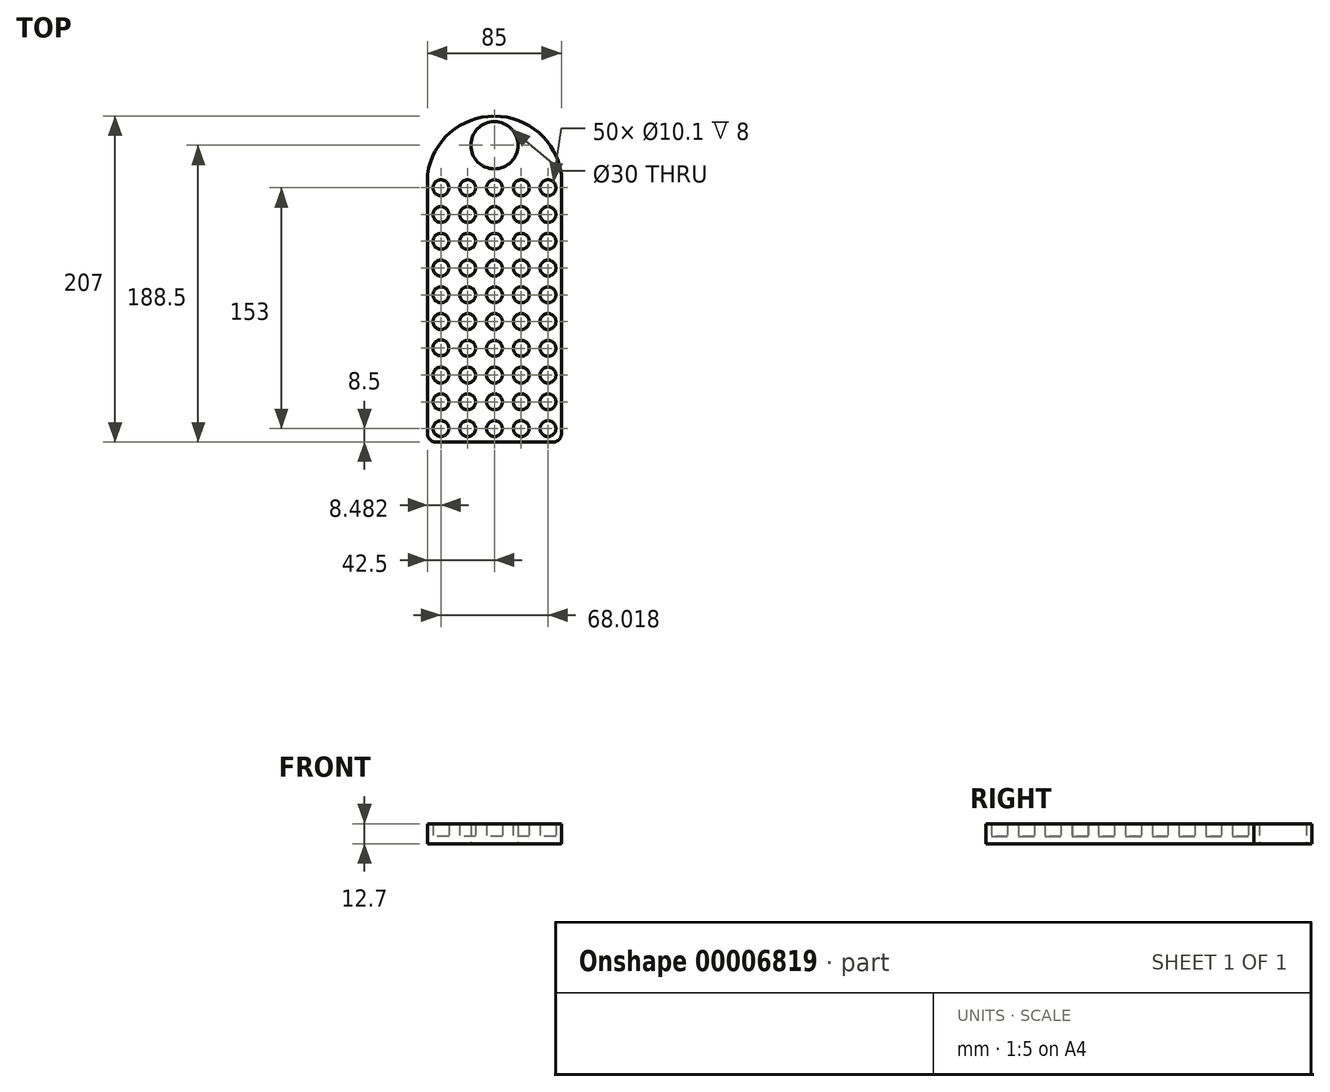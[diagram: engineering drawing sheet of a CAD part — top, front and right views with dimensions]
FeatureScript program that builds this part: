
annotation { "Feature Type Name" : "Feature", "Feature Type Description" : "" }
export const myFeature = defineFeature(function(context is Context, id is Id, definition is map)
    precondition{}
    {
        {
            var Q0;
            Q0=qCreatedBy(makeId("Top.planeOp"),FACE);
            var sketch = newSketch(context, id + "F0", { "sketchPlane" : qUnion([Q0])});
            skLineSegment(sketch, "E0", {"start": v(0, 0) * mm, "end": v(8.5, 0) * mm, "construction": true});
            skLineSegment(sketch, "E1", {"start": v(8.5, 0) * mm, "end": v(25.5, 0) * mm, "construction": true});
            skLineSegment(sketch, "E2", {"start": v(25.5, 0) * mm, "end": v(25.5, 0) * mm});
            skLineSegment(sketch, "E3", {"start": v(25.5, 0) * mm, "end": v(42.5, 0) * mm, "construction": true});
            skLineSegment(sketch, "E4", {"start": v(42.5, 0) * mm, "end": v(42.5, 0) * mm});
            skLineSegment(sketch, "E5", {"start": v(0, 0) * mm, "end": v(0, 8.5) * mm, "construction": true});
            skLineSegment(sketch, "E6", {"start": v(42.5, 0) * mm, "end": v(59.5, 0) * mm, "construction": true});
            skLineSegment(sketch, "E7", {"start": v(0, 8.5) * mm, "end": v(59.5, 8.5) * mm, "construction": true});
            skLineSegment(sketch, "E8", {"start": v(8.5, 0) * mm, "end": v(8.5, 8.5) * mm, "construction": true});
            skLineSegment(sketch, "E9", {"start": v(25.5, 0) * mm, "end": v(25.5, 8.5) * mm, "construction": true});
            skLineSegment(sketch, "E10", {"start": v(42.5, 0) * mm, "end": v(42.5, 8.5) * mm, "construction": true});
            skLineSegment(sketch, "E11", {"start": v(59.5, 0) * mm, "end": v(59.5, 8.5) * mm, "construction": true});
            skCircle(sketch, "E12", {"center": v(8.5, 8.5) * mm, "radius": 5.05 * mm});
            skLineSegment(sketch, "E13", {"start": v(59.5, 0) * mm, "end": v(76.5, 0) * mm, "construction": true});
            skLineSegment(sketch, "E14", {"start": v(59.5, 8.5) * mm, "end": v(76.5, 8.5) * mm, "construction": true});
            skLineSegment(sketch, "E15", {"start": v(76.5, 0) * mm, "end": v(76.5, 8.5) * mm, "construction": true});
            skCircle(sketch, "E16", {"center": v(25.5, 8.5) * mm, "radius": 5.05 * mm});
            skCircle(sketch, "E17", {"center": v(42.5, 8.5) * mm, "radius": 5.05 * mm});
            skCircle(sketch, "E18", {"center": v(59.5, 8.5) * mm, "radius": 5.05 * mm});
            skLineSegment(sketch, "E19", {"start": v(76.5, 0) * mm, "end": v(85, 0) * mm, "construction": true});
            skLineSegment(sketch, "E20", {"start": v(85, 8.5) * mm, "end": v(76.5, 8.5) * mm, "construction": true});
            skLineSegment(sketch, "E21", {"start": v(85, 0) * mm, "end": v(85, 8.5) * mm});
            skCircle(sketch, "E22", {"center": v(76.5, 8.5) * mm, "radius": 5.05 * mm});
            skLineSegment(sketch, "E23", {"start": v(0, 8.5) * mm, "end": v(0, 25.5) * mm, "construction": true});
            skLineSegment(sketch, "E24", {"start": v(0, 25.5) * mm, "end": v(85, 25.5) * mm, "construction": true});
            skLineSegment(sketch, "E25", {"start": v(8.5, 8.5) * mm, "end": v(8.5, 25.5) * mm, "construction": true});
            skLineSegment(sketch, "E26", {"start": v(25.5, 8.5) * mm, "end": v(25.5, 25.5) * mm, "construction": true});
            skLineSegment(sketch, "E27", {"start": v(42.5, 8.5) * mm, "end": v(42.5, 25.5) * mm, "construction": true});
            skLineSegment(sketch, "E28", {"start": v(59.5, 8.5) * mm, "end": v(59.5, 25.5) * mm, "construction": true});
            skLineSegment(sketch, "E29", {"start": v(76.5, 8.5) * mm, "end": v(76.5, 25.5) * mm, "construction": true});
            skLineSegment(sketch, "E30", {"start": v(85, 8.5) * mm, "end": v(85, 25.5) * mm, "construction": true});
            skCircle(sketch, "E31", {"center": v(8.5, 25.5) * mm, "radius": 5.05 * mm});
            skCircle(sketch, "E32", {"center": v(25.5, 25.5) * mm, "radius": 5.05 * mm});
            skCircle(sketch, "E33", {"center": v(42.5, 25.5) * mm, "radius": 5.05 * mm});
            skCircle(sketch, "E34", {"center": v(59.5, 25.5) * mm, "radius": 5.05 * mm});
            skCircle(sketch, "E35", {"center": v(76.5, 25.5) * mm, "radius": 5.05 * mm});
            skLineSegment(sketch, "E36", {"start": v(0, 25.5) * mm, "end": v(0, 42.5) * mm, "construction": true});
            skLineSegment(sketch, "E37", {"start": v(0, 42.5) * mm, "end": v(85, 42.5) * mm, "construction": true});
            skLineSegment(sketch, "E38", {"start": v(85, 25.5) * mm, "end": v(85, 42.5) * mm, "construction": true});
            skLineSegment(sketch, "E39", {"start": v(76.5, 25.5) * mm, "end": v(76.5, 42.5) * mm, "construction": true});
            skLineSegment(sketch, "E40", {"start": v(59.5, 25.5) * mm, "end": v(59.5, 42.5) * mm, "construction": true});
            skLineSegment(sketch, "E41", {"start": v(42.5, 25.5) * mm, "end": v(42.5, 42.5) * mm, "construction": true});
            skLineSegment(sketch, "E42", {"start": v(25.5, 25.5) * mm, "end": v(25.5, 42.5) * mm, "construction": true});
            skLineSegment(sketch, "E43", {"start": v(8.5, 25.5) * mm, "end": v(8.5, 42.5) * mm, "construction": true});
            skLineSegment(sketch, "E44", {"start": v(0, 42.5) * mm, "end": v(0, 59.5) * mm, "construction": true});
            skLineSegment(sketch, "E45", {"start": v(0, 59.5) * mm, "end": v(85, 59.5) * mm, "construction": true});
            skLineSegment(sketch, "E46", {"start": v(85, 42.5) * mm, "end": v(85, 59.5) * mm, "construction": true});
            skLineSegment(sketch, "E47", {"start": v(76.5, 42.5) * mm, "end": v(76.5, 59.5) * mm, "construction": true});
            skLineSegment(sketch, "E48", {"start": v(59.5, 42.5) * mm, "end": v(59.5, 59.5) * mm, "construction": true});
            skLineSegment(sketch, "E49", {"start": v(42.5, 42.5) * mm, "end": v(42.5, 59.5) * mm, "construction": true});
            skLineSegment(sketch, "E50", {"start": v(25.5, 42.5) * mm, "end": v(25.5, 59.5) * mm, "construction": true});
            skLineSegment(sketch, "E51", {"start": v(8.5, 42.5) * mm, "end": v(8.5, 59.5) * mm, "construction": true});
            skLineSegment(sketch, "E52", {"start": v(0, 59.5) * mm, "end": v(0, 76.5) * mm, "construction": true});
            skLineSegment(sketch, "E53", {"start": v(0, 76.5) * mm, "end": v(84.97, 76.5) * mm, "construction": true});
            skLineSegment(sketch, "E54", {"start": v(8.5, 59.5) * mm, "end": v(8.5, 76.5) * mm, "construction": true});
            skLineSegment(sketch, "E55", {"start": v(25.5, 59.5) * mm, "end": v(25.5, 76.5) * mm, "construction": true});
            skLineSegment(sketch, "E56", {"start": v(42.5, 59.5) * mm, "end": v(42.5, 76.5) * mm, "construction": true});
            skLineSegment(sketch, "E57", {"start": v(59.5, 59.5) * mm, "end": v(59.5, 76.5) * mm, "construction": true});
            skLineSegment(sketch, "E58", {"start": v(76.5, 59.5) * mm, "end": v(76.5, 76.5) * mm, "construction": true});
            skLineSegment(sketch, "E59", {"start": v(85, 59.5) * mm, "end": v(85, 76.5) * mm, "construction": true});
            skCircle(sketch, "E60", {"center": v(8.5, 42.5) * mm, "radius": 5.05 * mm});
            skCircle(sketch, "E61", {"center": v(8.48, 59.8) * mm, "radius": 5.05 * mm});
            skCircle(sketch, "E62", {"center": v(8.5, 76.5) * mm, "radius": 5.05 * mm});
            skCircle(sketch, "E63", {"center": v(25.5, 76.5) * mm, "radius": 5.05 * mm});
            skCircle(sketch, "E64", {"center": v(25.5, 59.5) * mm, "radius": 5.05 * mm});
            skCircle(sketch, "E65", {"center": v(25.5, 42.5) * mm, "radius": 5.05 * mm});
            skCircle(sketch, "E66", {"center": v(42.5, 76.5) * mm, "radius": 5.05 * mm});
            skCircle(sketch, "E67", {"center": v(42.5, 59.5) * mm, "radius": 5.05 * mm});
            skCircle(sketch, "E68", {"center": v(42.5, 42.5) * mm, "radius": 5.05 * mm});
            skCircle(sketch, "E69", {"center": v(59.5, 42.5) * mm, "radius": 5.05 * mm});
            skCircle(sketch, "E70", {"center": v(59.5, 59.5) * mm, "radius": 5.05 * mm});
            skCircle(sketch, "E71", {"center": v(59.5, 76.5) * mm, "radius": 5.05 * mm});
            skCircle(sketch, "E72", {"center": v(76.5, 76.5) * mm, "radius": 5.05 * mm});
            skCircle(sketch, "E73", {"center": v(76.5, 59.5) * mm, "radius": 5.05 * mm});
            skCircle(sketch, "E74", {"center": v(76.5, 42.5) * mm, "radius": 5.05 * mm});
            skLineSegment(sketch, "E75", {"start": v(0, 76.5) * mm, "end": v(0, 93.5) * mm, "construction": true});
            skLineSegment(sketch, "E76", {"start": v(0, 93.5) * mm, "end": v(85, 93.5) * mm, "construction": true});
            skLineSegment(sketch, "E77", {"start": v(8.5, 76.5) * mm, "end": v(8.5, 93.5) * mm, "construction": true});
            skLineSegment(sketch, "E78", {"start": v(25.5, 76.5) * mm, "end": v(25.5, 93.5) * mm, "construction": true});
            skLineSegment(sketch, "E79", {"start": v(42.5, 76.5) * mm, "end": v(42.5, 93.5) * mm, "construction": true});
            skLineSegment(sketch, "E80", {"start": v(59.5, 76.5) * mm, "end": v(59.5, 93.5) * mm, "construction": true});
            skLineSegment(sketch, "E81", {"start": v(76.38, 70.88) * mm, "end": v(76.5, 93.5) * mm, "construction": true});
            skLineSegment(sketch, "E82", {"start": v(76.5, 93.5) * mm, "end": v(76.5, 93.5) * mm});
            skLineSegment(sketch, "E83", {"start": v(85, 76.5) * mm, "end": v(85, 93.5) * mm, "construction": true});
            skLineSegment(sketch, "E84", {"start": v(0, 93.5) * mm, "end": v(0, 110.5) * mm, "construction": true});
            skLineSegment(sketch, "E85", {"start": v(0, 110.5) * mm, "end": v(85, 110.5) * mm, "construction": true});
            skLineSegment(sketch, "E86", {"start": v(8.5, 93.5) * mm, "end": v(8.5, 110.5) * mm, "construction": true});
            skLineSegment(sketch, "E87", {"start": v(25.5, 93.5) * mm, "end": v(25.5, 110.5) * mm, "construction": true});
            skLineSegment(sketch, "E88", {"start": v(42.5, 93.5) * mm, "end": v(42.5, 110.5) * mm, "construction": true});
            skLineSegment(sketch, "E89", {"start": v(59.5, 93.5) * mm, "end": v(59.5, 110.5) * mm, "construction": true});
            skLineSegment(sketch, "E90", {"start": v(76.5, 93.5) * mm, "end": v(76.5, 110.5) * mm, "construction": true});
            skLineSegment(sketch, "E91", {"start": v(85, 93.5) * mm, "end": v(85, 110.5) * mm, "construction": true});
            skLineSegment(sketch, "E92", {"start": v(0, 110.5) * mm, "end": v(0, 127.5) * mm, "construction": true});
            skLineSegment(sketch, "E93", {"start": v(0, 127.5) * mm, "end": v(85, 127.5) * mm, "construction": true});
            skLineSegment(sketch, "E94", {"start": v(8.5, 110.5) * mm, "end": v(8.5, 127.5) * mm, "construction": true});
            skLineSegment(sketch, "E95", {"start": v(25.5, 110.5) * mm, "end": v(25.5, 127.5) * mm, "construction": true});
            skLineSegment(sketch, "E96", {"start": v(42.5, 110.5) * mm, "end": v(42.5, 127.5) * mm, "construction": true});
            skLineSegment(sketch, "E97", {"start": v(59.5, 110.5) * mm, "end": v(59.5, 127.5) * mm, "construction": true});
            skLineSegment(sketch, "E98", {"start": v(76.5, 110.5) * mm, "end": v(76.5, 127.5) * mm, "construction": true});
            skLineSegment(sketch, "E99", {"start": v(85, 110.5) * mm, "end": v(85, 127.5) * mm, "construction": true});
            skLineSegment(sketch, "E100", {"start": v(0, 127.5) * mm, "end": v(0, 144.5) * mm, "construction": true});
            skLineSegment(sketch, "E101", {"start": v(0, 144.5) * mm, "end": v(85, 144.5) * mm, "construction": true});
            skLineSegment(sketch, "E102", {"start": v(8.5, 127.5) * mm, "end": v(8.5, 144.5) * mm, "construction": true});
            skLineSegment(sketch, "E103", {"start": v(25.5, 127.5) * mm, "end": v(25.5, 144.5) * mm, "construction": true});
            skLineSegment(sketch, "E104", {"start": v(42.5, 127.5) * mm, "end": v(42.5, 144.5) * mm, "construction": true});
            skLineSegment(sketch, "E105", {"start": v(59.5, 127.5) * mm, "end": v(59.5, 144.5) * mm, "construction": true});
            skLineSegment(sketch, "E106", {"start": v(76.5, 127.5) * mm, "end": v(76.5, 144.5) * mm, "construction": true});
            skLineSegment(sketch, "E107", {"start": v(85, 127.5) * mm, "end": v(85, 144.5) * mm, "construction": true});
            skLineSegment(sketch, "E108", {"start": v(0, 144.5) * mm, "end": v(0, 161.5) * mm, "construction": true});
            skLineSegment(sketch, "E109", {"start": v(0, 161.5) * mm, "end": v(85, 161.5) * mm, "construction": true});
            skLineSegment(sketch, "E110", {"start": v(8.5, 144.5) * mm, "end": v(8.5, 161.5) * mm, "construction": true});
            skLineSegment(sketch, "E111", {"start": v(25.5, 144.5) * mm, "end": v(25.5, 161.5) * mm, "construction": true});
            skLineSegment(sketch, "E112", {"start": v(42.5, 144.5) * mm, "end": v(42.5, 161.5) * mm, "construction": true});
            skLineSegment(sketch, "E113", {"start": v(59.5, 144.5) * mm, "end": v(59.5, 161.5) * mm, "construction": true});
            skLineSegment(sketch, "E114", {"start": v(76.5, 144.5) * mm, "end": v(76.5, 161.5) * mm, "construction": true});
            skLineSegment(sketch, "E115", {"start": v(85, 144.5) * mm, "end": v(85, 161.5) * mm, "construction": true});
            skCircle(sketch, "E116", {"center": v(8.5, 161.5) * mm, "radius": 5.05 * mm});
            skCircle(sketch, "E117", {"center": v(8.5, 144.5) * mm, "radius": 5.05 * mm});
            skCircle(sketch, "E118", {"center": v(8.5, 127.5) * mm, "radius": 5.05 * mm});
            skCircle(sketch, "E119", {"center": v(8.5, 110.5) * mm, "radius": 5.05 * mm});
            skCircle(sketch, "E120", {"center": v(8.5, 93.5) * mm, "radius": 5.05 * mm});
            skCircle(sketch, "E121", {"center": v(25.5, 93.5) * mm, "radius": 5.05 * mm});
            skCircle(sketch, "E122", {"center": v(25.5, 110.5) * mm, "radius": 5.05 * mm});
            skCircle(sketch, "E123", {"center": v(25.5, 127.5) * mm, "radius": 5.05 * mm});
            skCircle(sketch, "E124", {"center": v(25.5, 144.5) * mm, "radius": 5.05 * mm});
            skCircle(sketch, "E125", {"center": v(25.5, 161.5) * mm, "radius": 5.05 * mm});
            skCircle(sketch, "E126", {"center": v(42.5, 161.5) * mm, "radius": 5.05 * mm});
            skCircle(sketch, "E127", {"center": v(42.5, 144.5) * mm, "radius": 5.05 * mm});
            skCircle(sketch, "E128", {"center": v(42.5, 127.5) * mm, "radius": 5.05 * mm});
            skCircle(sketch, "E129", {"center": v(42.5, 110.5) * mm, "radius": 5.05 * mm});
            skCircle(sketch, "E130", {"center": v(42.5, 93.5) * mm, "radius": 5.05 * mm});
            skCircle(sketch, "E131", {"center": v(76.5, 93.5) * mm, "radius": 5.05 * mm});
            skCircle(sketch, "E132", {"center": v(59.5, 93.5) * mm, "radius": 5.05 * mm});
            skCircle(sketch, "E133", {"center": v(59.5, 110.5) * mm, "radius": 5.05 * mm});
            skCircle(sketch, "E134", {"center": v(76.5, 110.5) * mm, "radius": 5.05 * mm});
            skCircle(sketch, "E135", {"center": v(76.5, 127.5) * mm, "radius": 5.05 * mm});
            skCircle(sketch, "E136", {"center": v(59.5, 127.5) * mm, "radius": 5.05 * mm});
            skCircle(sketch, "E137", {"center": v(59.5, 144.5) * mm, "radius": 5.05 * mm});
            skCircle(sketch, "E138", {"center": v(76.5, 144.5) * mm, "radius": 5.05 * mm});
            skCircle(sketch, "E139", {"center": v(59.5, 161.5) * mm, "radius": 5.05 * mm});
            skCircle(sketch, "E140", {"center": v(76.5, 161.5) * mm, "radius": 5.05 * mm});
            skLineSegment(sketch, "E141", {"start": v(85, 161.5) * mm, "end": v(85, 170) * mm, "construction": true});
            skSolve(sketch);
        }
        {
            var Q0;
            Q0=qCreatedBy(makeId("Top.planeOp"),FACE);
            var sketch = newSketch(context, id + "F1", { "sketchPlane" : qUnion([Q0])});
            skLineSegment(sketch, "E142.bottom", {"start": v(5, 0) * mm, "end": v(80, 0) * mm});
            skLineSegment(sketch, "E142.top", {"start": v(0, 170) * mm, "end": v(85, 170) * mm, "construction": true});
            skLineSegment(sketch, "E142.left", {"start": v(0, 5) * mm, "end": v(0, 170) * mm});
            skLineSegment(sketch, "E142.right", {"start": v(85, 5) * mm, "end": v(85, 170) * mm});
            skPoint(sketch, "E143.visualSharp", {"position": v(85, 0) * mm});
            skArc(sketch, "E143.filletArc", {"start": v(80, 0) * mm, "mid": v(83.54, 1.46) * mm, "end": v(85, 5) * mm});
            skPoint(sketch, "E144.visualSharp", {"position": v(0, 0) * mm});
            skArc(sketch, "E144.filletArc", {"start": v(0, 5) * mm, "mid": v(1.46, 1.46) * mm, "end": v(5, 0) * mm});
            skLineSegment(sketch, "E145", {"start": v(42.5, 170) * mm, "end": v(42.5, 188.5) * mm, "construction": true});
            skCircle(sketch, "E146", {"center": v(42.5, 188.5) * mm, "radius": 15 * mm});
            skLineSegment(sketch, "E147", {"start": v(42.5, 188.5) * mm, "end": v(42.5, 203.5) * mm, "construction": true});
            skLineSegment(sketch, "E148", {"start": v(42.5, 203.5) * mm, "end": v(42.5, 207) * mm, "construction": true});
            skLineSegment(sketch, "E149", {"start": v(42.5, 170) * mm, "end": v(42.5, 173.5) * mm, "construction": true});
            skArc(sketch, "E150", {"start": v(85, 170) * mm, "mid": v(42.5, 207) * mm, "end": v(0, 170) * mm});
            skSolve(sketch);
        }
        {
            var Q0;
            Q0 = qSketchRegion(id + "F0", true);
            extrude(context, id + "F2", {"entities" : qUnion([Q0]), "depth" : 4.7 * mm});
        }
        {
            var Q0;
            Q0=makeQuery(id+"F2.opExtrude","CAP_FACE",FACE,{"disambiguationData":[OSD([sQuery(id+"F0.wireOp",EDGE,"E17")])],"isStart":false});
            var Q1;
            Q1=makeQuery(id+"F2.opExtrude","CAP_FACE",FACE,{"disambiguationData":[OSD([sQuery(id+"F0.wireOp",EDGE,"E18")])],"isStart":false});
            var Q2;
            Q2=makeQuery(id+"F2.opExtrude","CAP_FACE",FACE,{"disambiguationData":[OSD([sQuery(id+"F0.wireOp",EDGE,"E22")])],"isStart":false});
            var Q3;
            Q3=makeQuery(id+"F2.opExtrude","CAP_FACE",FACE,{"disambiguationData":[OSD([sQuery(id+"F0.wireOp",EDGE,"E35")])],"isStart":false});
            var Q4;
            Q4=makeQuery(id+"F2.opExtrude","CAP_FACE",FACE,{"disambiguationData":[OSD([sQuery(id+"F0.wireOp",EDGE,"E34")])],"isStart":false});
            var Q5;
            Q5=makeQuery(id+"F2.opExtrude","CAP_FACE",FACE,{"disambiguationData":[OSD([sQuery(id+"F0.wireOp",EDGE,"E33")])],"isStart":false});
            var Q6;
            Q6=makeQuery(id+"F2.opExtrude","CAP_FACE",FACE,{"disambiguationData":[OSD([sQuery(id+"F0.wireOp",EDGE,"E32")])],"isStart":false});
            var Q7;
            Q7=makeQuery(id+"F2.opExtrude","CAP_FACE",FACE,{"disambiguationData":[OSD([sQuery(id+"F0.wireOp",EDGE,"E16")])],"isStart":false});
            var Q8;
            Q8=makeQuery(id+"F2.opExtrude","CAP_FACE",FACE,{"disambiguationData":[OSD([sQuery(id+"F0.wireOp",EDGE,"E12")])],"isStart":false});
            var Q9;
            Q9=makeQuery(id+"F2.opExtrude","CAP_FACE",FACE,{"disambiguationData":[OSD([sQuery(id+"F0.wireOp",EDGE,"E31")])],"isStart":false});
            var Q10;
            Q10=makeQuery(id+"F2.opExtrude","CAP_FACE",FACE,{"disambiguationData":[OSD([sQuery(id+"F0.wireOp",EDGE,"E60")])],"isStart":false});
            var Q11;
            Q11=makeQuery(id+"F2.opExtrude","CAP_FACE",FACE,{"disambiguationData":[OSD([sQuery(id+"F0.wireOp",EDGE,"E65")])],"isStart":false});
            var Q12;
            Q12=makeQuery(id+"F2.opExtrude","CAP_FACE",FACE,{"disambiguationData":[OSD([sQuery(id+"F0.wireOp",EDGE,"E68")])],"isStart":false});
            var Q13;
            Q13=makeQuery(id+"F2.opExtrude","CAP_FACE",FACE,{"disambiguationData":[OSD([sQuery(id+"F0.wireOp",EDGE,"E69")])],"isStart":false});
            var Q14;
            Q14=makeQuery(id+"F2.opExtrude","CAP_FACE",FACE,{"disambiguationData":[OSD([sQuery(id+"F0.wireOp",EDGE,"E74")])],"isStart":false});
            var Q15;
            Q15=makeQuery(id+"F2.opExtrude","CAP_FACE",FACE,{"disambiguationData":[OSD([sQuery(id+"F0.wireOp",EDGE,"E73")])],"isStart":false});
            var Q16;
            Q16=makeQuery(id+"F2.opExtrude","CAP_FACE",FACE,{"disambiguationData":[OSD([sQuery(id+"F0.wireOp",EDGE,"E70")])],"isStart":false});
            var Q17;
            Q17=makeQuery(id+"F2.opExtrude","CAP_FACE",FACE,{"disambiguationData":[OSD([sQuery(id+"F0.wireOp",EDGE,"E67")])],"isStart":false});
            var Q18;
            Q18=makeQuery(id+"F2.opExtrude","CAP_FACE",FACE,{"disambiguationData":[OSD([sQuery(id+"F0.wireOp",EDGE,"E64")])],"isStart":false});
            var Q19;
            Q19=makeQuery(id+"F2.opExtrude","CAP_FACE",FACE,{"disambiguationData":[OSD([sQuery(id+"F0.wireOp",EDGE,"E61")])],"isStart":false});
            var Q20;
            Q20=makeQuery(id+"F2.opExtrude","CAP_FACE",FACE,{"disambiguationData":[OSD([sQuery(id+"F0.wireOp",EDGE,"E62")])],"isStart":false});
            var Q21;
            Q21=makeQuery(id+"F2.opExtrude","CAP_FACE",FACE,{"disambiguationData":[OSD([sQuery(id+"F0.wireOp",EDGE,"E120")])],"isStart":false});
            var Q22;
            Q22=makeQuery(id+"F2.opExtrude","CAP_FACE",FACE,{"disambiguationData":[OSD([sQuery(id+"F0.wireOp",EDGE,"E119")])],"isStart":false});
            var Q23;
            Q23=makeQuery(id+"F2.opExtrude","CAP_FACE",FACE,{"disambiguationData":[OSD([sQuery(id+"F0.wireOp",EDGE,"E118")])],"isStart":false});
            var Q24;
            Q24=makeQuery(id+"F2.opExtrude","CAP_FACE",FACE,{"disambiguationData":[OSD([sQuery(id+"F0.wireOp",EDGE,"E117")])],"isStart":false});
            var Q25;
            Q25=makeQuery(id+"F2.opExtrude","CAP_FACE",FACE,{"disambiguationData":[OSD([sQuery(id+"F0.wireOp",EDGE,"E116")])],"isStart":false});
            var Q26;
            Q26=makeQuery(id+"F2.opExtrude","CAP_FACE",FACE,{"disambiguationData":[OSD([sQuery(id+"F0.wireOp",EDGE,"E125")])],"isStart":false});
            var Q27;
            Q27=makeQuery(id+"F2.opExtrude","CAP_FACE",FACE,{"disambiguationData":[OSD([sQuery(id+"F0.wireOp",EDGE,"E124")])],"isStart":false});
            var Q28;
            Q28=makeQuery(id+"F2.opExtrude","CAP_FACE",FACE,{"disambiguationData":[OSD([sQuery(id+"F0.wireOp",EDGE,"E123")])],"isStart":false});
            var Q29;
            Q29=makeQuery(id+"F2.opExtrude","CAP_FACE",FACE,{"disambiguationData":[OSD([sQuery(id+"F0.wireOp",EDGE,"E122")])],"isStart":false});
            var Q30;
            Q30=makeQuery(id+"F2.opExtrude","CAP_FACE",FACE,{"disambiguationData":[OSD([sQuery(id+"F0.wireOp",EDGE,"E121")])],"isStart":false});
            var Q31;
            Q31=makeQuery(id+"F2.opExtrude","CAP_FACE",FACE,{"disambiguationData":[OSD([sQuery(id+"F0.wireOp",EDGE,"E63")])],"isStart":false});
            var Q32;
            Q32=makeQuery(id+"F2.opExtrude","CAP_FACE",FACE,{"disambiguationData":[OSD([sQuery(id+"F0.wireOp",EDGE,"E66")])],"isStart":false});
            var Q33;
            Q33=makeQuery(id+"F2.opExtrude","CAP_FACE",FACE,{"disambiguationData":[OSD([sQuery(id+"F0.wireOp",EDGE,"E71")])],"isStart":false});
            var Q34;
            Q34=makeQuery(id+"F2.opExtrude","CAP_FACE",FACE,{"disambiguationData":[OSD([sQuery(id+"F0.wireOp",EDGE,"E72")])],"isStart":false});
            var Q35;
            Q35=makeQuery(id+"F2.opExtrude","CAP_FACE",FACE,{"disambiguationData":[OSD([sQuery(id+"F0.wireOp",EDGE,"E131")])],"isStart":false});
            var Q36;
            Q36=makeQuery(id+"F2.opExtrude","CAP_FACE",FACE,{"disambiguationData":[OSD([sQuery(id+"F0.wireOp",EDGE,"E132")])],"isStart":false});
            var Q37;
            Q37=makeQuery(id+"F2.opExtrude","CAP_FACE",FACE,{"disambiguationData":[OSD([sQuery(id+"F0.wireOp",EDGE,"E130")])],"isStart":false});
            var Q38;
            Q38=makeQuery(id+"F2.opExtrude","CAP_FACE",FACE,{"disambiguationData":[OSD([sQuery(id+"F0.wireOp",EDGE,"E129")])],"isStart":false});
            var Q39;
            Q39=makeQuery(id+"F2.opExtrude","CAP_FACE",FACE,{"disambiguationData":[OSD([sQuery(id+"F0.wireOp",EDGE,"E133")])],"isStart":false});
            var Q40;
            Q40=makeQuery(id+"F2.opExtrude","CAP_FACE",FACE,{"disambiguationData":[OSD([sQuery(id+"F0.wireOp",EDGE,"E134")])],"isStart":false});
            var Q41;
            Q41=makeQuery(id+"F2.opExtrude","CAP_FACE",FACE,{"disambiguationData":[OSD([sQuery(id+"F0.wireOp",EDGE,"E135")])],"isStart":false});
            var Q42;
            Q42=makeQuery(id+"F2.opExtrude","CAP_FACE",FACE,{"disambiguationData":[OSD([sQuery(id+"F0.wireOp",EDGE,"E136")])],"isStart":false});
            var Q43;
            Q43=makeQuery(id+"F2.opExtrude","CAP_FACE",FACE,{"disambiguationData":[OSD([sQuery(id+"F0.wireOp",EDGE,"E128")])],"isStart":false});
            var Q44;
            Q44=makeQuery(id+"F2.opExtrude","CAP_FACE",FACE,{"disambiguationData":[OSD([sQuery(id+"F0.wireOp",EDGE,"E127")])],"isStart":false});
            var Q45;
            Q45=makeQuery(id+"F2.opExtrude","CAP_FACE",FACE,{"disambiguationData":[OSD([sQuery(id+"F0.wireOp",EDGE,"E126")])],"isStart":false});
            var Q46;
            Q46=makeQuery(id+"F2.opExtrude","CAP_FACE",FACE,{"disambiguationData":[OSD([sQuery(id+"F0.wireOp",EDGE,"E139")])],"isStart":false});
            var Q47;
            Q47=makeQuery(id+"F2.opExtrude","CAP_FACE",FACE,{"disambiguationData":[OSD([sQuery(id+"F0.wireOp",EDGE,"E137")])],"isStart":false});
            var Q48;
            Q48=makeQuery(id+"F2.opExtrude","CAP_FACE",FACE,{"disambiguationData":[OSD([sQuery(id+"F0.wireOp",EDGE,"E138")])],"isStart":false});
            var Q49;
            Q49=makeQuery(id+"F2.opExtrude","CAP_FACE",FACE,{"disambiguationData":[OSD([sQuery(id+"F0.wireOp",EDGE,"E140")])],"isStart":false});
            extrude(context, id + "F3", {"entities" : qUnion([Q0, Q1, Q2, Q3, Q4, Q5, Q6, Q7, Q8, Q9, Q10, Q11, Q12, Q13, Q14, Q15, Q16, Q17, Q18, Q19, Q20, Q21, Q22, Q23, Q24, Q25, Q26, Q27, Q28, Q29, Q30, Q31, Q32, Q33, Q34, Q35, Q36, Q37, Q38, Q39, Q40, Q41, Q42, Q43, Q44, Q45, Q46, Q47, Q48, Q49]), "depth" : 8 * mm});
        }
        {
            var Q0;
            Q0=makeQuery(id+"F2.opExtrude","SWEPT_BODY",BODY,{"disambiguationData":[OSD([sQuery(id+"F0.wireOp",EDGE,"E12")])]});
            var Q1;
            Q1=makeQuery(id+"F2.opExtrude","SWEPT_BODY",BODY,{"disambiguationData":[OSD([sQuery(id+"F0.wireOp",EDGE,"E16")])]});
            var Q2;
            Q2=makeQuery(id+"F2.opExtrude","SWEPT_BODY",BODY,{"disambiguationData":[OSD([sQuery(id+"F0.wireOp",EDGE,"E17")])]});
            var Q3;
            Q3=makeQuery(id+"F2.opExtrude","SWEPT_BODY",BODY,{"disambiguationData":[OSD([sQuery(id+"F0.wireOp",EDGE,"E18")])]});
            var Q4;
            Q4=makeQuery(id+"F2.opExtrude","SWEPT_BODY",BODY,{"disambiguationData":[OSD([sQuery(id+"F0.wireOp",EDGE,"E22")])]});
            var Q5;
            Q5=makeQuery(id+"F2.opExtrude","SWEPT_BODY",BODY,{"disambiguationData":[OSD([sQuery(id+"F0.wireOp",EDGE,"E31")])]});
            var Q6;
            Q6=makeQuery(id+"F2.opExtrude","SWEPT_BODY",BODY,{"disambiguationData":[OSD([sQuery(id+"F0.wireOp",EDGE,"E32")])]});
            var Q7;
            Q7=makeQuery(id+"F2.opExtrude","SWEPT_BODY",BODY,{"disambiguationData":[OSD([sQuery(id+"F0.wireOp",EDGE,"E33")])]});
            var Q8;
            Q8=makeQuery(id+"F2.opExtrude","SWEPT_BODY",BODY,{"disambiguationData":[OSD([sQuery(id+"F0.wireOp",EDGE,"E34")])]});
            var Q9;
            Q9=makeQuery(id+"F2.opExtrude","SWEPT_BODY",BODY,{"disambiguationData":[OSD([sQuery(id+"F0.wireOp",EDGE,"E35")])]});
            var Q10;
            Q10=makeQuery(id+"F2.opExtrude","SWEPT_BODY",BODY,{"disambiguationData":[OSD([sQuery(id+"F0.wireOp",EDGE,"E60")])]});
            var Q11;
            Q11=makeQuery(id+"F2.opExtrude","SWEPT_BODY",BODY,{"disambiguationData":[OSD([sQuery(id+"F0.wireOp",EDGE,"E61")])]});
            var Q12;
            Q12=makeQuery(id+"F2.opExtrude","SWEPT_BODY",BODY,{"disambiguationData":[OSD([sQuery(id+"F0.wireOp",EDGE,"E62")])]});
            var Q13;
            Q13=makeQuery(id+"F2.opExtrude","SWEPT_BODY",BODY,{"disambiguationData":[OSD([sQuery(id+"F0.wireOp",EDGE,"E63")])]});
            var Q14;
            Q14=makeQuery(id+"F2.opExtrude","SWEPT_BODY",BODY,{"disambiguationData":[OSD([sQuery(id+"F0.wireOp",EDGE,"E64")])]});
            var Q15;
            Q15=makeQuery(id+"F2.opExtrude","SWEPT_BODY",BODY,{"disambiguationData":[OSD([sQuery(id+"F0.wireOp",EDGE,"E65")])]});
            var Q16;
            Q16=makeQuery(id+"F2.opExtrude","SWEPT_BODY",BODY,{"disambiguationData":[OSD([sQuery(id+"F0.wireOp",EDGE,"E66")])]});
            var Q17;
            Q17=makeQuery(id+"F2.opExtrude","SWEPT_BODY",BODY,{"disambiguationData":[OSD([sQuery(id+"F0.wireOp",EDGE,"E67")])]});
            var Q18;
            Q18=makeQuery(id+"F2.opExtrude","SWEPT_BODY",BODY,{"disambiguationData":[OSD([sQuery(id+"F0.wireOp",EDGE,"E68")])]});
            var Q19;
            Q19=makeQuery(id+"F2.opExtrude","SWEPT_BODY",BODY,{"disambiguationData":[OSD([sQuery(id+"F0.wireOp",EDGE,"E69")])]});
            var Q20;
            Q20=makeQuery(id+"F2.opExtrude","SWEPT_BODY",BODY,{"disambiguationData":[OSD([sQuery(id+"F0.wireOp",EDGE,"E70")])]});
            var Q21;
            Q21=makeQuery(id+"F2.opExtrude","SWEPT_BODY",BODY,{"disambiguationData":[OSD([sQuery(id+"F0.wireOp",EDGE,"E71")])]});
            var Q22;
            Q22=makeQuery(id+"F2.opExtrude","SWEPT_BODY",BODY,{"disambiguationData":[OSD([sQuery(id+"F0.wireOp",EDGE,"E72")])]});
            var Q23;
            Q23=makeQuery(id+"F2.opExtrude","SWEPT_BODY",BODY,{"disambiguationData":[OSD([sQuery(id+"F0.wireOp",EDGE,"E73")])]});
            var Q24;
            Q24=makeQuery(id+"F2.opExtrude","SWEPT_BODY",BODY,{"disambiguationData":[OSD([sQuery(id+"F0.wireOp",EDGE,"E74")])]});
            var Q25;
            Q25=makeQuery(id+"F2.opExtrude","SWEPT_BODY",BODY,{"disambiguationData":[OSD([sQuery(id+"F0.wireOp",EDGE,"E116")])]});
            var Q26;
            Q26=makeQuery(id+"F2.opExtrude","SWEPT_BODY",BODY,{"disambiguationData":[OSD([sQuery(id+"F0.wireOp",EDGE,"E117")])]});
            var Q27;
            Q27=makeQuery(id+"F2.opExtrude","SWEPT_BODY",BODY,{"disambiguationData":[OSD([sQuery(id+"F0.wireOp",EDGE,"E118")])]});
            var Q28;
            Q28=makeQuery(id+"F2.opExtrude","SWEPT_BODY",BODY,{"disambiguationData":[OSD([sQuery(id+"F0.wireOp",EDGE,"E119")])]});
            var Q29;
            Q29=makeQuery(id+"F2.opExtrude","SWEPT_BODY",BODY,{"disambiguationData":[OSD([sQuery(id+"F0.wireOp",EDGE,"E120")])]});
            var Q30;
            Q30=makeQuery(id+"F2.opExtrude","SWEPT_BODY",BODY,{"disambiguationData":[OSD([sQuery(id+"F0.wireOp",EDGE,"E121")])]});
            var Q31;
            Q31=makeQuery(id+"F2.opExtrude","SWEPT_BODY",BODY,{"disambiguationData":[OSD([sQuery(id+"F0.wireOp",EDGE,"E122")])]});
            var Q32;
            Q32=makeQuery(id+"F2.opExtrude","SWEPT_BODY",BODY,{"disambiguationData":[OSD([sQuery(id+"F0.wireOp",EDGE,"E123")])]});
            var Q33;
            Q33=makeQuery(id+"F2.opExtrude","SWEPT_BODY",BODY,{"disambiguationData":[OSD([sQuery(id+"F0.wireOp",EDGE,"E124")])]});
            var Q34;
            Q34=makeQuery(id+"F2.opExtrude","SWEPT_BODY",BODY,{"disambiguationData":[OSD([sQuery(id+"F0.wireOp",EDGE,"E125")])]});
            var Q35;
            Q35=makeQuery(id+"F2.opExtrude","SWEPT_BODY",BODY,{"disambiguationData":[OSD([sQuery(id+"F0.wireOp",EDGE,"E126")])]});
            var Q36;
            Q36=makeQuery(id+"F2.opExtrude","SWEPT_BODY",BODY,{"disambiguationData":[OSD([sQuery(id+"F0.wireOp",EDGE,"E127")])]});
            var Q37;
            Q37=makeQuery(id+"F2.opExtrude","SWEPT_BODY",BODY,{"disambiguationData":[OSD([sQuery(id+"F0.wireOp",EDGE,"E128")])]});
            var Q38;
            Q38=makeQuery(id+"F2.opExtrude","SWEPT_BODY",BODY,{"disambiguationData":[OSD([sQuery(id+"F0.wireOp",EDGE,"E129")])]});
            var Q39;
            Q39=makeQuery(id+"F2.opExtrude","SWEPT_BODY",BODY,{"disambiguationData":[OSD([sQuery(id+"F0.wireOp",EDGE,"E130")])]});
            var Q40;
            Q40=makeQuery(id+"F2.opExtrude","SWEPT_BODY",BODY,{"disambiguationData":[OSD([sQuery(id+"F0.wireOp",EDGE,"E131")])]});
            var Q41;
            Q41=makeQuery(id+"F2.opExtrude","SWEPT_BODY",BODY,{"disambiguationData":[OSD([sQuery(id+"F0.wireOp",EDGE,"E132")])]});
            var Q42;
            Q42=makeQuery(id+"F2.opExtrude","SWEPT_BODY",BODY,{"disambiguationData":[OSD([sQuery(id+"F0.wireOp",EDGE,"E133")])]});
            var Q43;
            Q43=makeQuery(id+"F2.opExtrude","SWEPT_BODY",BODY,{"disambiguationData":[OSD([sQuery(id+"F0.wireOp",EDGE,"E134")])]});
            var Q44;
            Q44=makeQuery(id+"F2.opExtrude","SWEPT_BODY",BODY,{"disambiguationData":[OSD([sQuery(id+"F0.wireOp",EDGE,"E135")])]});
            var Q45;
            Q45=makeQuery(id+"F2.opExtrude","SWEPT_BODY",BODY,{"disambiguationData":[OSD([sQuery(id+"F0.wireOp",EDGE,"E136")])]});
            var Q46;
            Q46=makeQuery(id+"F2.opExtrude","SWEPT_BODY",BODY,{"disambiguationData":[OSD([sQuery(id+"F0.wireOp",EDGE,"E137")])]});
            var Q47;
            Q47=makeQuery(id+"F2.opExtrude","SWEPT_BODY",BODY,{"disambiguationData":[OSD([sQuery(id+"F0.wireOp",EDGE,"E138")])]});
            var Q48;
            Q48=makeQuery(id+"F2.opExtrude","SWEPT_BODY",BODY,{"disambiguationData":[OSD([sQuery(id+"F0.wireOp",EDGE,"E139")])]});
            var Q49;
            Q49=makeQuery(id+"F2.opExtrude","SWEPT_BODY",BODY,{"disambiguationData":[OSD([sQuery(id+"F0.wireOp",EDGE,"E140")])]});
            deleteBodies(context, id + "F4", {"entities" : qUnion([Q0, Q1, Q2, Q3, Q4, Q5, Q6, Q7, Q8, Q9, Q10, Q11, Q12, Q13, Q14, Q15, Q16, Q17, Q18, Q19, Q20, Q21, Q22, Q23, Q24, Q25, Q26, Q27, Q28, Q29, Q30, Q31, Q32, Q33, Q34, Q35, Q36, Q37, Q38, Q39, Q40, Q41, Q42, Q43, Q44, Q45, Q46, Q47, Q48, Q49])});
        }
        {
            var Q0;
            Q0=makeQuery(id+"F1.imprint","IMPRINT",FACE,{"disambiguationData":[TD([[makeQuery(id+"F1.imprint","IMPRINT",EDGE,{"derivedFrom":sQuery(id+"F1.wireOp",EDGE,"E142.bottom")}),1.0]])]});
            extrude(context, id + "F5", {"entities" : qUnion([Q0]), "depth" : 12.7 * mm});
        }
        {
            var Q0;
            Q0=makeQuery(id+"F3.opExtrude","SWEPT_BODY",BODY,{"disambiguationData":[OSD([sQuery(id+"F0.wireOp",EDGE,"E12")])]});
            var Q1;
            Q1=makeQuery(id+"F3.opExtrude","SWEPT_BODY",BODY,{"disambiguationData":[OSD([sQuery(id+"F0.wireOp",EDGE,"E16")])]});
            var Q2;
            Q2=makeQuery(id+"F3.opExtrude","SWEPT_BODY",BODY,{"disambiguationData":[OSD([sQuery(id+"F0.wireOp",EDGE,"E17")])]});
            var Q3;
            Q3=makeQuery(id+"F3.opExtrude","SWEPT_BODY",BODY,{"disambiguationData":[OSD([sQuery(id+"F0.wireOp",EDGE,"E18")])]});
            var Q4;
            Q4=makeQuery(id+"F3.opExtrude","SWEPT_BODY",BODY,{"disambiguationData":[OSD([sQuery(id+"F0.wireOp",EDGE,"E22")])]});
            var Q5;
            Q5=makeQuery(id+"F3.opExtrude","SWEPT_BODY",BODY,{"disambiguationData":[OSD([sQuery(id+"F0.wireOp",EDGE,"E31")])]});
            var Q6;
            Q6=makeQuery(id+"F3.opExtrude","SWEPT_BODY",BODY,{"disambiguationData":[OSD([sQuery(id+"F0.wireOp",EDGE,"E32")])]});
            var Q7;
            Q7=makeQuery(id+"F3.opExtrude","SWEPT_BODY",BODY,{"disambiguationData":[OSD([sQuery(id+"F0.wireOp",EDGE,"E33")])]});
            var Q8;
            Q8=makeQuery(id+"F3.opExtrude","SWEPT_BODY",BODY,{"disambiguationData":[OSD([sQuery(id+"F0.wireOp",EDGE,"E34")])]});
            var Q9;
            Q9=makeQuery(id+"F3.opExtrude","SWEPT_BODY",BODY,{"disambiguationData":[OSD([sQuery(id+"F0.wireOp",EDGE,"E35")])]});
            var Q10;
            Q10=makeQuery(id+"F3.opExtrude","SWEPT_BODY",BODY,{"disambiguationData":[OSD([sQuery(id+"F0.wireOp",EDGE,"E60")])]});
            var Q11;
            Q11=makeQuery(id+"F3.opExtrude","SWEPT_BODY",BODY,{"disambiguationData":[OSD([sQuery(id+"F0.wireOp",EDGE,"E61")])]});
            var Q12;
            Q12=makeQuery(id+"F3.opExtrude","SWEPT_BODY",BODY,{"disambiguationData":[OSD([sQuery(id+"F0.wireOp",EDGE,"E62")])]});
            var Q13;
            Q13=makeQuery(id+"F3.opExtrude","SWEPT_BODY",BODY,{"disambiguationData":[OSD([sQuery(id+"F0.wireOp",EDGE,"E63")])]});
            var Q14;
            Q14=makeQuery(id+"F3.opExtrude","SWEPT_BODY",BODY,{"disambiguationData":[OSD([sQuery(id+"F0.wireOp",EDGE,"E64")])]});
            var Q15;
            Q15=makeQuery(id+"F3.opExtrude","SWEPT_BODY",BODY,{"disambiguationData":[OSD([sQuery(id+"F0.wireOp",EDGE,"E65")])]});
            var Q16;
            Q16=makeQuery(id+"F3.opExtrude","SWEPT_BODY",BODY,{"disambiguationData":[OSD([sQuery(id+"F0.wireOp",EDGE,"E66")])]});
            var Q17;
            Q17=makeQuery(id+"F3.opExtrude","SWEPT_BODY",BODY,{"disambiguationData":[OSD([sQuery(id+"F0.wireOp",EDGE,"E67")])]});
            var Q18;
            Q18=makeQuery(id+"F3.opExtrude","SWEPT_BODY",BODY,{"disambiguationData":[OSD([sQuery(id+"F0.wireOp",EDGE,"E68")])]});
            var Q19;
            Q19=makeQuery(id+"F3.opExtrude","SWEPT_BODY",BODY,{"disambiguationData":[OSD([sQuery(id+"F0.wireOp",EDGE,"E69")])]});
            var Q20;
            Q20=makeQuery(id+"F3.opExtrude","SWEPT_BODY",BODY,{"disambiguationData":[OSD([sQuery(id+"F0.wireOp",EDGE,"E70")])]});
            var Q21;
            Q21=makeQuery(id+"F3.opExtrude","SWEPT_BODY",BODY,{"disambiguationData":[OSD([sQuery(id+"F0.wireOp",EDGE,"E71")])]});
            var Q22;
            Q22=makeQuery(id+"F3.opExtrude","SWEPT_BODY",BODY,{"disambiguationData":[OSD([sQuery(id+"F0.wireOp",EDGE,"E72")])]});
            var Q23;
            Q23=makeQuery(id+"F3.opExtrude","SWEPT_BODY",BODY,{"disambiguationData":[OSD([sQuery(id+"F0.wireOp",EDGE,"E73")])]});
            var Q24;
            Q24=makeQuery(id+"F3.opExtrude","SWEPT_BODY",BODY,{"disambiguationData":[OSD([sQuery(id+"F0.wireOp",EDGE,"E74")])]});
            var Q25;
            Q25=makeQuery(id+"F3.opExtrude","SWEPT_BODY",BODY,{"disambiguationData":[OSD([sQuery(id+"F0.wireOp",EDGE,"E116")])]});
            var Q26;
            Q26=makeQuery(id+"F3.opExtrude","SWEPT_BODY",BODY,{"disambiguationData":[OSD([sQuery(id+"F0.wireOp",EDGE,"E117")])]});
            var Q27;
            Q27=makeQuery(id+"F3.opExtrude","SWEPT_BODY",BODY,{"disambiguationData":[OSD([sQuery(id+"F0.wireOp",EDGE,"E118")])]});
            var Q28;
            Q28=makeQuery(id+"F3.opExtrude","SWEPT_BODY",BODY,{"disambiguationData":[OSD([sQuery(id+"F0.wireOp",EDGE,"E119")])]});
            var Q29;
            Q29=makeQuery(id+"F3.opExtrude","SWEPT_BODY",BODY,{"disambiguationData":[OSD([sQuery(id+"F0.wireOp",EDGE,"E120")])]});
            var Q30;
            Q30=makeQuery(id+"F3.opExtrude","SWEPT_BODY",BODY,{"disambiguationData":[OSD([sQuery(id+"F0.wireOp",EDGE,"E121")])]});
            var Q31;
            Q31=makeQuery(id+"F3.opExtrude","SWEPT_BODY",BODY,{"disambiguationData":[OSD([sQuery(id+"F0.wireOp",EDGE,"E122")])]});
            var Q32;
            Q32=makeQuery(id+"F3.opExtrude","SWEPT_BODY",BODY,{"disambiguationData":[OSD([sQuery(id+"F0.wireOp",EDGE,"E123")])]});
            var Q33;
            Q33=makeQuery(id+"F3.opExtrude","SWEPT_BODY",BODY,{"disambiguationData":[OSD([sQuery(id+"F0.wireOp",EDGE,"E124")])]});
            var Q34;
            Q34=makeQuery(id+"F3.opExtrude","SWEPT_BODY",BODY,{"disambiguationData":[OSD([sQuery(id+"F0.wireOp",EDGE,"E125")])]});
            var Q35;
            Q35=makeQuery(id+"F3.opExtrude","SWEPT_BODY",BODY,{"disambiguationData":[OSD([sQuery(id+"F0.wireOp",EDGE,"E126")])]});
            var Q36;
            Q36=makeQuery(id+"F3.opExtrude","SWEPT_BODY",BODY,{"disambiguationData":[OSD([sQuery(id+"F0.wireOp",EDGE,"E127")])]});
            var Q37;
            Q37=makeQuery(id+"F3.opExtrude","SWEPT_BODY",BODY,{"disambiguationData":[OSD([sQuery(id+"F0.wireOp",EDGE,"E128")])]});
            var Q38;
            Q38=makeQuery(id+"F3.opExtrude","SWEPT_BODY",BODY,{"disambiguationData":[OSD([sQuery(id+"F0.wireOp",EDGE,"E129")])]});
            var Q39;
            Q39=makeQuery(id+"F3.opExtrude","SWEPT_BODY",BODY,{"disambiguationData":[OSD([sQuery(id+"F0.wireOp",EDGE,"E130")])]});
            var Q40;
            Q40=makeQuery(id+"F3.opExtrude","SWEPT_BODY",BODY,{"disambiguationData":[OSD([sQuery(id+"F0.wireOp",EDGE,"E131")])]});
            var Q41;
            Q41=makeQuery(id+"F3.opExtrude","SWEPT_BODY",BODY,{"disambiguationData":[OSD([sQuery(id+"F0.wireOp",EDGE,"E132")])]});
            var Q42;
            Q42=makeQuery(id+"F3.opExtrude","SWEPT_BODY",BODY,{"disambiguationData":[OSD([sQuery(id+"F0.wireOp",EDGE,"E133")])]});
            var Q43;
            Q43=makeQuery(id+"F3.opExtrude","SWEPT_BODY",BODY,{"disambiguationData":[OSD([sQuery(id+"F0.wireOp",EDGE,"E134")])]});
            var Q44;
            Q44=makeQuery(id+"F3.opExtrude","SWEPT_BODY",BODY,{"disambiguationData":[OSD([sQuery(id+"F0.wireOp",EDGE,"E135")])]});
            var Q45;
            Q45=makeQuery(id+"F3.opExtrude","SWEPT_BODY",BODY,{"disambiguationData":[OSD([sQuery(id+"F0.wireOp",EDGE,"E136")])]});
            var Q46;
            Q46=makeQuery(id+"F3.opExtrude","SWEPT_BODY",BODY,{"disambiguationData":[OSD([sQuery(id+"F0.wireOp",EDGE,"E137")])]});
            var Q47;
            Q47=makeQuery(id+"F3.opExtrude","SWEPT_BODY",BODY,{"disambiguationData":[OSD([sQuery(id+"F0.wireOp",EDGE,"E138")])]});
            var Q48;
            Q48=makeQuery(id+"F3.opExtrude","SWEPT_BODY",BODY,{"disambiguationData":[OSD([sQuery(id+"F0.wireOp",EDGE,"E139")])]});
            var Q49;
            Q49=makeQuery(id+"F3.opExtrude","SWEPT_BODY",BODY,{"disambiguationData":[OSD([sQuery(id+"F0.wireOp",EDGE,"E140")])]});
            var Q50;
            Q50=makeQuery(id+"F5.opExtrude","SWEPT_BODY",BODY,{"disambiguationData":[OSD([sQuery(id+"F1.wireOp",EDGE,"E142.bottom"),sQuery(id+"F1.wireOp",EDGE,"E142.left"),sQuery(id+"F1.wireOp",EDGE,"E142.right"),sQuery(id+"F1.wireOp",EDGE,"E143.filletArc"),sQuery(id+"F1.wireOp",EDGE,"E144.filletArc"),sQuery(id+"F1.wireOp",EDGE,"E146"),sQuery(id+"F1.wireOp",EDGE,"E150")])]});
            booleanBodies(context, id + "F6", {"operationType" : BooleanOperationType.SUBTRACTION, "tools" : qUnion([Q0, Q1, Q2, Q3, Q4, Q5, Q6, Q7, Q8, Q9, Q10, Q11, Q12, Q13, Q14, Q15, Q16, Q17, Q18, Q19, Q20, Q21, Q22, Q23, Q24, Q25, Q26, Q27, Q28, Q29, Q30, Q31, Q32, Q33, Q34, Q35, Q36, Q37, Q38, Q39, Q40, Q41, Q42, Q43, Q44, Q45, Q46, Q47, Q48, Q49]), "targets" : qUnion([Q50])});
        }
    });
